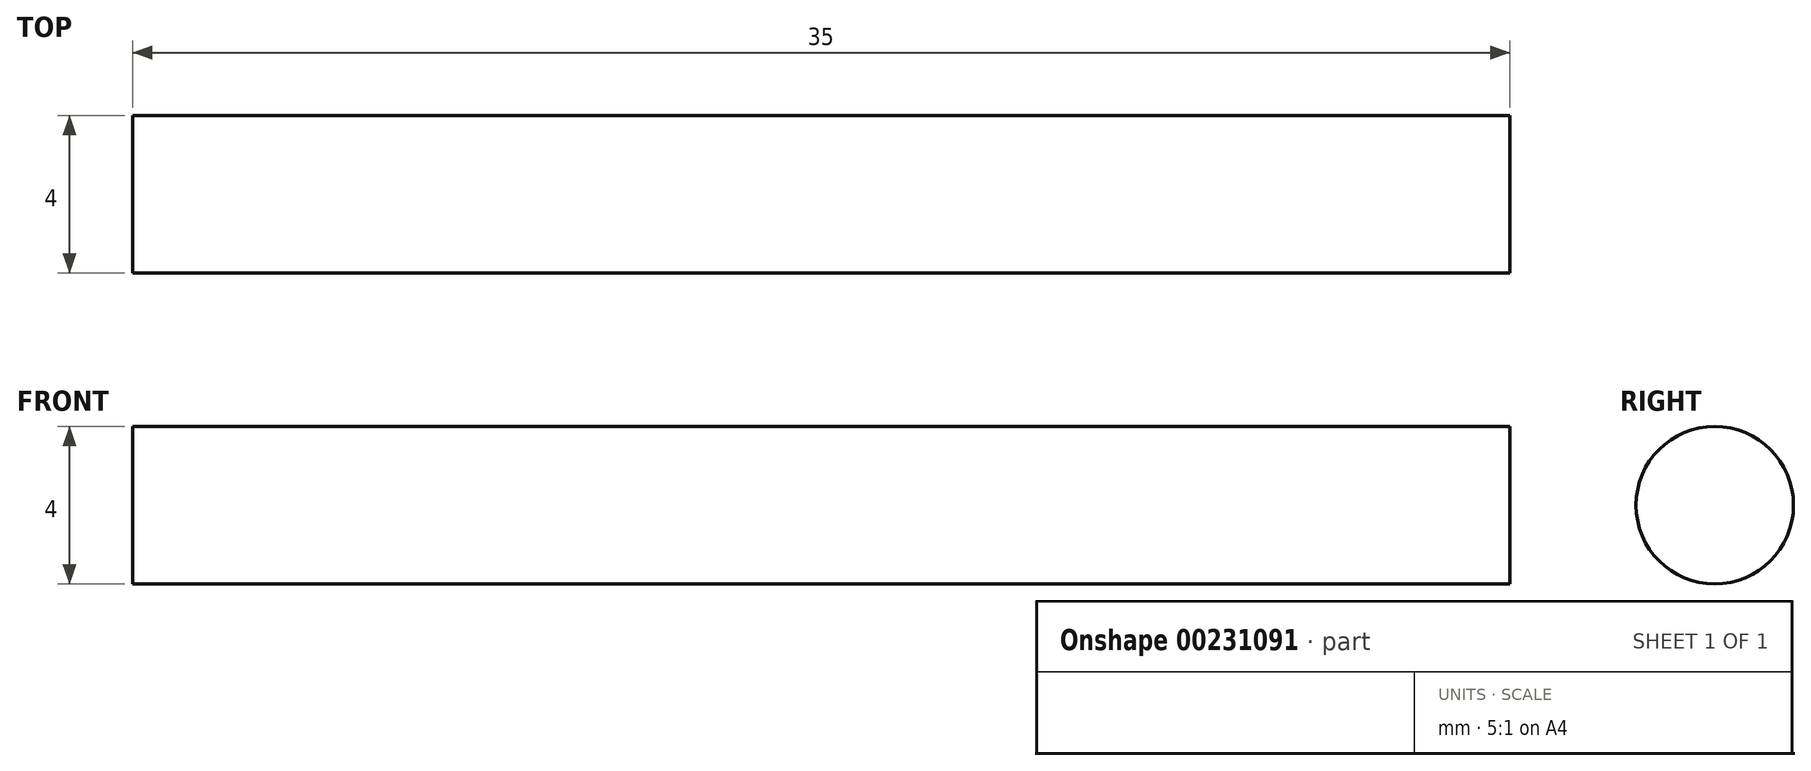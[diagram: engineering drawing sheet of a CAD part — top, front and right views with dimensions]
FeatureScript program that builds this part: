
annotation { "Feature Type Name" : "Feature", "Feature Type Description" : "" }
export const myFeature = defineFeature(function(context is Context, id is Id, definition is map)
    precondition{}
    {
        {
            var Q0;
            Q0=qCreatedBy(makeId("Front.planeOp"),FACE);
            var sketch = newSketch(context, id + "F0", { "sketchPlane" : qUnion([Q0])});
            skLineSegment(sketch, "E0", {"start": v(0, 0) * mm, "end": v(0, 2) * mm});
            skLineSegment(sketch, "E1", {"start": v(0, 2) * mm, "end": v(35, 2) * mm});
            skLineSegment(sketch, "E2", {"start": v(35, 2) * mm, "end": v(35, 0) * mm});
            skLineSegment(sketch, "E3", {"start": v(35, 0) * mm, "end": v(0, 0) * mm});
            skSolve(sketch);
        }
        {
            var Q0;
            Q0 = qSketchRegion(id + "F0", true);
            var Q1;
            Q1=sQuery(id+"F0.wireOp",EDGE,"E3");
            revolve(context, id + "F1", {"entities" : qUnion([Q0]), "axis" : qUnion([Q1]), "revolveType" : RevolveType.FULL});
        }
    });
